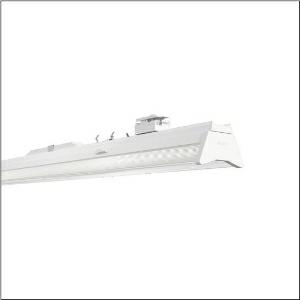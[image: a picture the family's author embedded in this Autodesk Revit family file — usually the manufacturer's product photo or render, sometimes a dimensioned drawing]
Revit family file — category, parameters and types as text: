
# Revit family: licross_r__21_performance_ho_52td16mn4e5m_6ed4
name_source: partatom
category: Lighting Fixtures
units: mm (PartAtom-declared; Revit-internal decimal feet)

## family parameters
Cut with Voids When Loaded = No
Host = Face
Light Source = No
Part Type = Normal
Room Calculation Point = No
Round Connector Dimension = Use Diameter
Shared = No

## types (1)
- --- (1 x LED, 14970 lm, 83.2 W, 4000K)
    Apparent Load = 83 VA
    CIE Flux Codes = 63 87 95 78 100
    Color Rendering = 80
    Color Temperature = 4000K
    Default Elevation = 1800 mm
    Description = Licross® 21 Performance HO, luminaire insert, of sheet steel, galvanised, coil coated, white, length: 1.500mm, width: 120mm, height: 123mm, LED rated luminous flux: 14.970lm, light colour: 840, control gear: ON/OFF Multilumen, with plug, 3-pole, with phase selection, mains connection: 220..240V, AC, 50/60Hz, rated input power: 83W, halogen-free wiring, primary light control with lens, of plastic, primary optical cover: cover, of PMMA, light emission: direct/indirect distribution, primary light characteristic: symmetric, protection rating (complete): IP54, insulation class (complete): insulation class I (protective earthing), certification: CE, ENEC, UKCA, protection symbol: D if used in an environment with non-conductive dust loads with corresponding accessories, impact resistance: IK06, permissible ambient temperature for indoor applications: -35..+35°C, corresponds to IFS (International Featured Standards) requirements for safety and quality in the food industry, reducing of maximum allowable ambient temperature of 5°C with ceiling mounting, LABS conformity tested according to VDMA 24364:2018-05, packaging unit: 1 piece
    Height = 114 mm
    Lamp = 1 x LED
    Lamp Light Flux = 14970 lm
    Lamp Power = 83.2 W
    Lamp count = 1
    Length = 1500 mm
    Luminous efficacy = 180 lm/W
    Manufacturer = Siteco
    ModVariant = No
    Model = 52TD16MN4E5M
    Mounting Place = Ceiling
    Mounting Type = Pendant
    Number of Poles = 1
    OnlyDefault = Yes
    Power Factor = 1
    Product Name = Licross® 21 Performance HO
    Product group = luminaire insert
    ProductGroupID = 902
    Protection Class = Protection class I
    Protection Degree = IP 54
    RLX_Detail_Level = 1
    RLX_Emergency_Light_Flux = 0 lm
    RLX_Emergency_Type = 0
    RLX_Emergency_Type_DB = No
    RlxData = <blob elided: 31713 chars, md5=272251c3>
    Socket = socket
    Standby Power = 0 W
    System Light Flux = 14970 lm
    System Power = 83 W
    Type Comments = factory setting: luminous flux: 100 % | (A | C | E) | 195 mA
    Type Image = l_1256138.jpg
    URL = http://relux.com
    VarID = @adj_109240
    Voltage = 0 V
    Weight = 0.00 kg
    Width = 120 mm

## geometry (parser evidence)
native form markers: Blend x4, Sweep x12
no freeform markers — native parametric forms only
